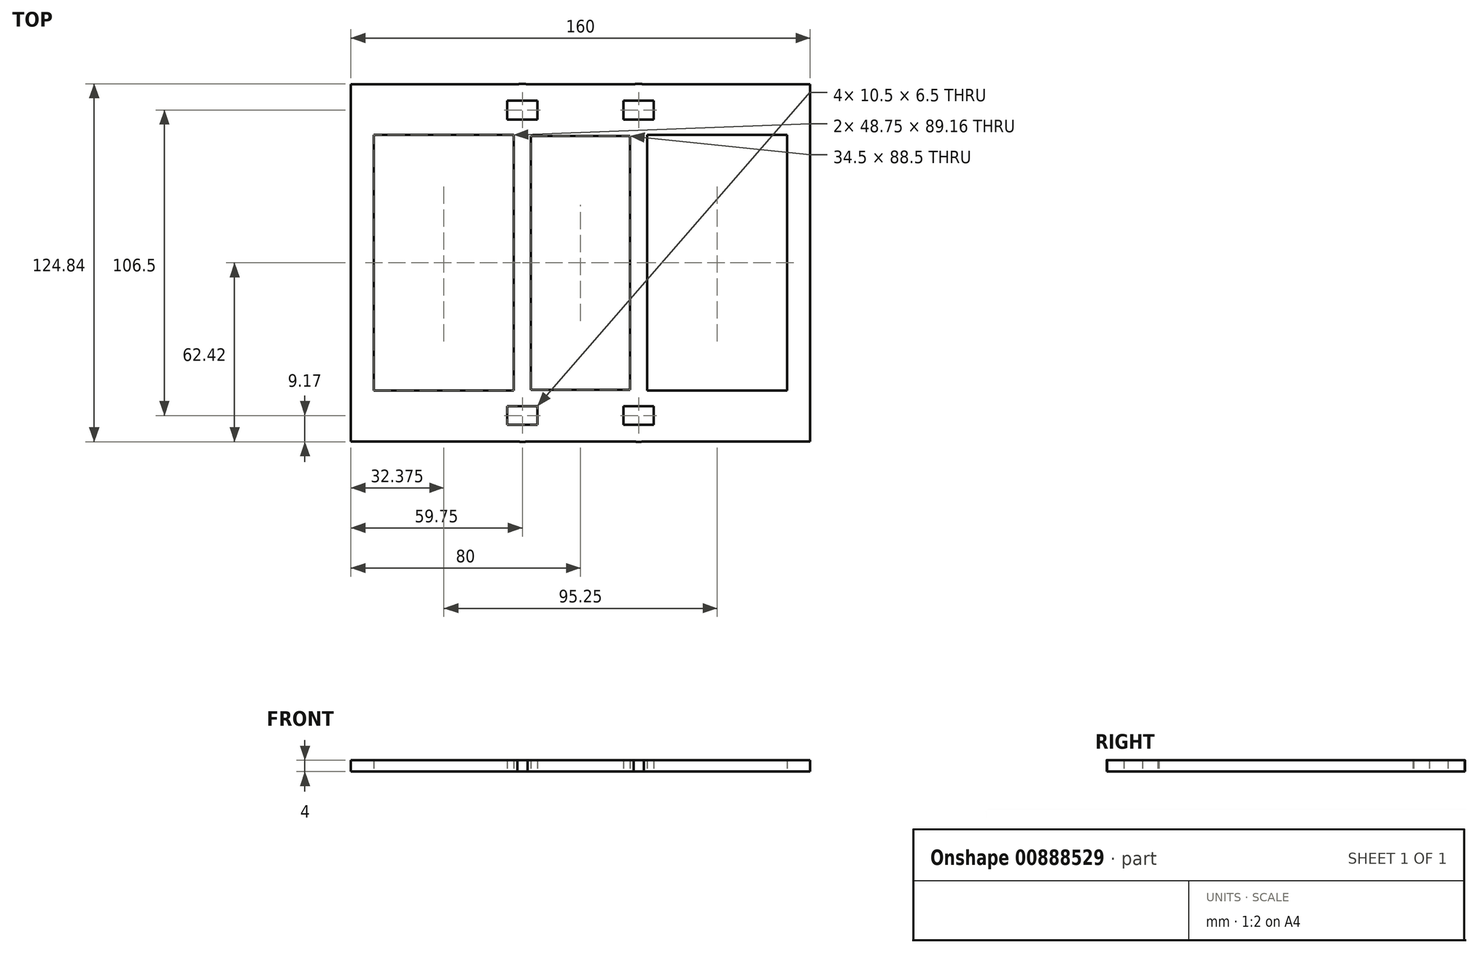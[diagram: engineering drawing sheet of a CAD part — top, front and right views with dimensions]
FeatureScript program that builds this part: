
annotation { "Feature Type Name" : "Feature", "Feature Type Description" : "" }
export const myFeature = defineFeature(function(context is Context, id is Id, definition is map)
    precondition{}
    {
        {
            var Q0;
            Q0=qCreatedBy(makeId("Top.planeOp"),FACE);
            var sketch = newSketch(context, id + "F0", { "sketchPlane" : qUnion([Q0])});
            skLineSegment(sketch, "E0.bottom", {"start": v(-25.5, 56.5) * mm, "end": v(-15, 56.5) * mm});
            skLineSegment(sketch, "E0.top", {"start": v(-25.5, 50) * mm, "end": v(-15, 50) * mm});
            skLineSegment(sketch, "E0.left", {"start": v(-25.5, 56.5) * mm, "end": v(-25.5, 50) * mm});
            skLineSegment(sketch, "E0.right", {"start": v(-15, 56.5) * mm, "end": v(-15, 50) * mm});
            skLineSegment(sketch, "E1", {"start": v(-18.47, 62.25) * mm, "end": v(0, 62.25) * mm});
            skLineSegment(sketch, "E2", {"start": v(-18.47, 44.25) * mm, "end": v(0, 44.25) * mm});
            skLineSegment(sketch, "E3", {"start": v(-17.25, 44.58) * mm, "end": v(-17.25, 0) * mm});
            skLineSegment(sketch, "E4", {"start": v(-23.25, 44.58) * mm, "end": v(-23.25, 0) * mm});
            skCircle(sketch, "E5", {"center": v(-20.25, 53.25) * mm, "radius": 9.17 * mm});
            skLineSegment(sketch, "E6", {"start": v(-25.5, 50) * mm, "end": v(-15, 56.5) * mm, "construction": true});
            skLineSegment(sketch, "E7", {"start": v(-23.25, 0) * mm, "end": v(-17.25, 0) * mm});
            skLineSegment(sketch, "E8", {"start": v(0, 62.25) * mm, "end": v(0, 44.25) * mm});
            skLineSegment(sketch, "E9.bottom", {"start": v(0, 62.25) * mm, "end": v(-80, 62.25) * mm});
            skLineSegment(sketch, "E9.top", {"start": v(0, 44.58) * mm, "end": v(-80, 44.58) * mm});
            skLineSegment(sketch, "E9.left", {"start": v(0, 62.25) * mm, "end": v(0, 44.58) * mm});
            skLineSegment(sketch, "E9.right", {"start": v(-80, 62.25) * mm, "end": v(-80, 44.58) * mm});
            skLineSegment(sketch, "E10.bottom", {"start": v(-80, 62.25) * mm, "end": v(-72, 62.25) * mm});
            skLineSegment(sketch, "E10.top", {"start": v(-80, 0) * mm, "end": v(-72, 0) * mm});
            skLineSegment(sketch, "E10.left", {"start": v(-80, 62.25) * mm, "end": v(-80, 0) * mm});
            skLineSegment(sketch, "E10.right", {"start": v(-72, 62.25) * mm, "end": v(-72, 0) * mm});
            skSolve(sketch);
        }
        {
            var Q0;
            Q0=qSketchRegion(id+"F0",true);
            extrude(context, id + "F1", {"entities" : qUnion([Q0]), "endBound" : BoundingType.SYMMETRIC, "depth" : 4 * mm});
        }
        {
            var Q0;
            Q0=makeQuery(id+"F1.opExtrude","SWEPT_BODY",BODY,{"disambiguationData":[OSD([sQuery(id+"F0.wireOp",EDGE,"E0.bottom"),sQuery(id+"F0.wireOp",EDGE,"E0.top"),sQuery(id+"F0.wireOp",EDGE,"E0.left"),sQuery(id+"F0.wireOp",EDGE,"E0.right"),sQuery(id+"F0.wireOp",EDGE,"E1"),sQuery(id+"F0.wireOp",EDGE,"E2"),sQuery(id+"F0.wireOp",EDGE,"E3"),sQuery(id+"F0.wireOp",EDGE,"E4"),sQuery(id+"F0.wireOp",EDGE,"E5"),sQuery(id+"F0.wireOp",EDGE,"885d0998-28b2-41a1-97cd-30c48dccc7c7"),sQuery(id+"F0.wireOp",EDGE,"cf62aa76-d4d9-4a14-965e-934055f67eda"),sQuery(id+"F0.wireOp",EDGE,"63d2a611-28e1-420f-b2a1-a0f714a071c9"),sQuery(id+"F0.wireOp",EDGE,"E7"),sQuery(id+"F0.wireOp",EDGE,"E8")])]});
            var Q1;
            Q1=makeQuery(id+"F1.opExtrude","SWEPT_FACE",FACE,{"disambiguationData":[OSD([sQuery(id+"F0.wireOp",EDGE,"E8")])]});
            mirror(context, id + "F2", {"operationType" : NewBodyOperationType.ADD, "entities" : qUnion([Q0]), "mirrorPlane" : qUnion([Q1])});
        }
        {
            var Q0;
            Q0=makeQuery(id+"F1.opExtrude","SWEPT_BODY",BODY,{"disambiguationData":[OSD([sQuery(id+"F0.wireOp",EDGE,"E0.bottom"),sQuery(id+"F0.wireOp",EDGE,"E0.top"),sQuery(id+"F0.wireOp",EDGE,"E0.left"),sQuery(id+"F0.wireOp",EDGE,"E0.right"),sQuery(id+"F0.wireOp",EDGE,"E1"),sQuery(id+"F0.wireOp",EDGE,"E2"),sQuery(id+"F0.wireOp",EDGE,"E3"),sQuery(id+"F0.wireOp",EDGE,"E4"),sQuery(id+"F0.wireOp",EDGE,"E5"),sQuery(id+"F0.wireOp",EDGE,"885d0998-28b2-41a1-97cd-30c48dccc7c7"),sQuery(id+"F0.wireOp",EDGE,"cf62aa76-d4d9-4a14-965e-934055f67eda"),sQuery(id+"F0.wireOp",EDGE,"63d2a611-28e1-420f-b2a1-a0f714a071c9"),sQuery(id+"F0.wireOp",EDGE,"E7"),sQuery(id+"F0.wireOp",EDGE,"E8")])]});
            var Q1;
            Q1=makeQuery(id+"F1.opExtrude","SWEPT_FACE",FACE,{"disambiguationData":[OSD([sQuery(id+"F0.wireOp",EDGE,"E7")])]});
            mirror(context, id + "F3", {"operationType" : NewBodyOperationType.ADD, "entities" : qUnion([Q0]), "mirrorPlane" : qUnion([Q1])});
        }
    });
